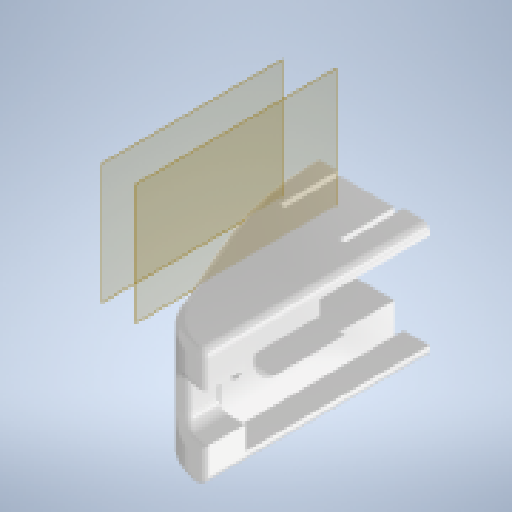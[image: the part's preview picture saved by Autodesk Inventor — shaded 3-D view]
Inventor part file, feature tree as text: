
AUTODESK INVENTOR PART (.ipt)
format: ipt  version: 2025 (Build 290162010, 162A)  size: 526,336 bytes
history: native  units: mm
features: extrude x8, sketch x7, other x4, hole x3, fillet x3, plane x2, reference x2, mirror x1
ambient origin geometry x8: Origin, YZ Plane, XZ Plane, XY Plane, X Axis, Y Axis, Z Axis, Center Point
bodies: Volumenkörper1 (feature_tree)
feature tree (30):
  sketch  "Skizze1"  dims[d0=5.0mm d1=45.0mm d2=30.0mm d3=0.0mm]
  extrude  "Extrusion1"  Depth=30.0mm TaperAngle=0.0deg
  hole  "Bohrung2"  [1 undecoded]
  extrude  "Extrusion2"  [1 undecoded]
  plane  "Arbeitsebene1"
  hole  "Bohrung4"  [1 undecoded]
  extrude  "Extrusion3"  Depth=2.0mm
  plane  "Arbeitsebene2"
  hole  "Bohrung5"  [1 undecoded]
  extrude  "Extrusion4"  Depth=2.0mm
  extrude  "Extrusion5"  Depth=2.0mm TaperAngle=0.0deg
  extrude  "Extrusion6"  [1 undecoded]
  fillet  "Rundung2"  Radius=7.8mm
  sketch  "Skizze13"  dims[d41=12.0mm d42=0.0mm d43=0.0mm d44=3.2mm d45=6.0mm d46=6.3mm d47=2.0mm d48=90.0deg d49=8.0mm d50=20.594885mm d51=12.0mm d52=8.0mm d53=0.0mm d54=-19.5mm d56=7.8mm d57=1.0mm d58=0.0mm d59=2.0mm d60=0.0mm d61=12.0mm d62=8.5mm d63=0.0mm d65=0.5mm d66=3.0mm d67=1.0mm d68=0.0mm d69=8.5mm d70=0.0mm d71=3.0mm d72=15.0mm d73=15.0mm d75=35.0mm d76=2.0mm d77=0.0mm d78=2.0mm]
  extrude  "Extrusion7"  Depth=2.0mm TaperAngle=0.0deg
  extrude  "Extrusion8"  Depth=2.0mm TaperAngle=0.0deg
  fillet  "Rundung3"  Radius=12.0mm
  mirror  "Spiegeln1"
  fillet  "Rundung4"  Radius=8.5mm
  reference  "Referenz1"
  sketch  "Skizze3"  dims[d4=15.0mm d14=6.5mm]
  reference  "Referenz3"
  sketch  "Skizze5"  dims[d15=5.0mm]
  sketch  "Skizze7"  dims[d16=1.567mm d17=8.0mm d18=4.0mm d19=2.0mm d20=90.0deg d21=10.0mm d22=20.594885mm d30=-10.0mm]
  sketch  "Skizze8"  dims[d31=15.0mm d32=15.0mm]
  sketch  "Skizze9"  dims[d33=3.2mm d34=6.0mm d35=6.3mm d36=2.0mm d37=90.0deg d38=8.0mm d39=20.594885mm d40=14.0mm]
  other  "<userpath>\GIT\HDVKBM\CAD\Krandemonstrator\Demonstrator.iam"
  other  "Demonstrator.iam"
  other  "Träger:1"
  other  "AS 1112 (2) - Metrisch M4  Typ 5:1"
note: 5 required parameter values undecoded (feature->parameter linkage not recoverable at this tier; creation-order binding heuristic only, values carry confidence <= 0.55)
